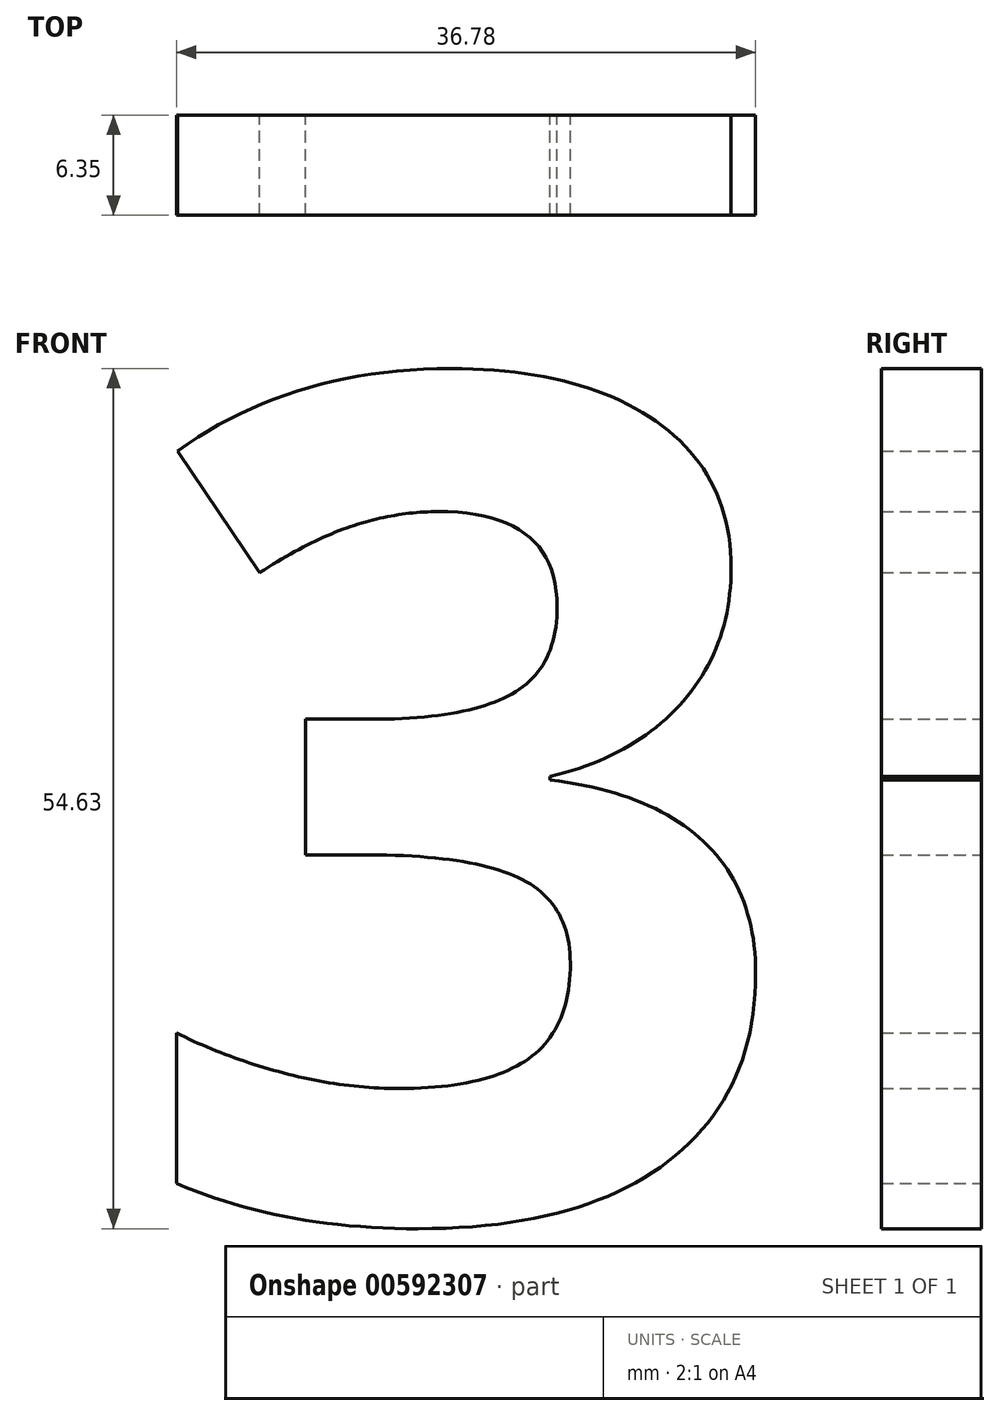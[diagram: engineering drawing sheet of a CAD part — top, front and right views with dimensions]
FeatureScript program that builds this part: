
annotation { "Feature Type Name" : "Feature", "Feature Type Description" : "" }
export const myFeature = defineFeature(function(context is Context, id is Id, definition is map)
    precondition{}
    {
        {
            var Q0;
            Q0=qCreatedBy(makeId("Front.planeOp"),FACE);
            var sketch = newSketch(context, id + "F0", { "sketchPlane" : qUnion([Q0])});
            skText(sketch, "E0", { "text": "3", "fontName": "OpenSans-Bold.ttf"});
            const initialGuessF0  = {"E0": [-0.04463, -0.0161, 1, 0, 0.0536]};
            skSetInitialGuess(sketch, initialGuessF0);
            skSolve(sketch);
        }
        {
            var Q0;
            Q0 = qSketchRegion(id + "F0", true);
            extrude(context, id + "F1", {"entities" : qUnion([Q0]), "depth" : 6.35 * mm, "offsetDistance" : 25.4 * mm});
        }
    });
